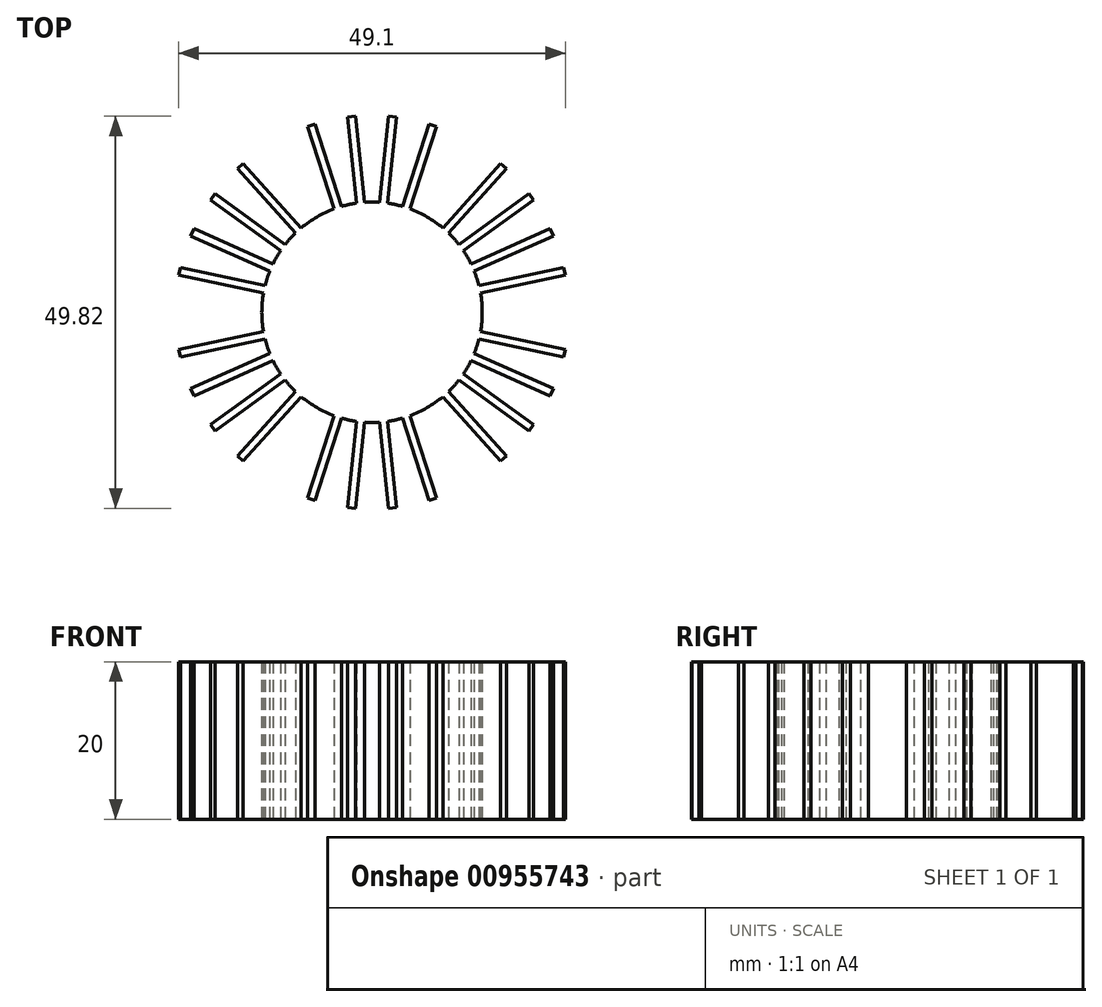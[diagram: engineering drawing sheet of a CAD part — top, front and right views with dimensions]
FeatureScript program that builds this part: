
annotation { "Feature Type Name" : "Feature", "Feature Type Description" : "" }
export const myFeature = defineFeature(function(context is Context, id is Id, definition is map)
    precondition{}
    {
        {
            var Q0;
            Q0=qCreatedBy(makeId("Top.planeOp"),FACE);
            var sketch = newSketch(context, id + "F0", { "sketchPlane" : qUnion([Q0])});
            skCircle(sketch, "E0", {"center": v(0, 0) * mm, "radius": 14 * mm});
            skLineSegment(sketch, "E1.bottom", {"start": v(0.97, 13.97) * mm, "end": v(1.96, 13.86) * mm});
            skLineSegment(sketch, "E1.top", {"start": v(2.12, 24.9) * mm, "end": v(3.1, 24.8) * mm});
            skLineSegment(sketch, "E1.left", {"start": v(0.97, 13.97) * mm, "end": v(2.12, 24.9) * mm});
            skLineSegment(sketch, "E1.right", {"start": v(1.96, 13.86) * mm, "end": v(3.1, 24.8) * mm});
            skLineSegment(sketch, "E2", {"start": v(0, 0) * mm, "end": v(0, 14) * mm});
            skLineSegment(sketch, "E3.1.0", {"start": v(-0.97, 13.97) * mm, "end": v(-2.12, 24.9) * mm});
            skLineSegment(sketch, "E3.1.1", {"start": v(-1.96, 13.86) * mm, "end": v(-3.1, 24.8) * mm});
            skLineSegment(sketch, "E3.1.2", {"start": v(-3.1, 24.8) * mm, "end": v(-2.12, 24.9) * mm});
            skLineSegment(sketch, "E3.2.0", {"start": v(-3.85, 13.46) * mm, "end": v(-7.25, 23.92) * mm});
            skLineSegment(sketch, "E3.2.1", {"start": v(-4.8, 13.15) * mm, "end": v(-8.2, 23.61) * mm});
            skLineSegment(sketch, "E3.2.2", {"start": v(-8.2, 23.61) * mm, "end": v(-7.25, 23.92) * mm});
            skLineSegment(sketch, "E3.4.0", {"start": v(-9, 10.73) * mm, "end": v(-16.35, 18.9) * mm});
            skLineSegment(sketch, "E3.4.1", {"start": v(-9.73, 10.06) * mm, "end": v(-17.1, 18.24) * mm});
            skLineSegment(sketch, "E3.4.2", {"start": v(-17.1, 18.24) * mm, "end": v(-16.35, 18.9) * mm});
            skLineSegment(sketch, "E3.5.0", {"start": v(-11.03, 8.63) * mm, "end": v(-19.92, 15.1) * mm});
            skLineSegment(sketch, "E3.5.1", {"start": v(-11.61, 7.82) * mm, "end": v(-20.51, 14.28) * mm});
            skLineSegment(sketch, "E3.5.2", {"start": v(-20.51, 14.28) * mm, "end": v(-19.92, 15.1) * mm});
            skLineSegment(sketch, "E3.6.0", {"start": v(-12.58, 6.15) * mm, "end": v(-22.63, 10.62) * mm});
            skLineSegment(sketch, "E3.6.1", {"start": v(-12.98, 5.23) * mm, "end": v(-23.03, 9.7) * mm});
            skLineSegment(sketch, "E3.6.2", {"start": v(-23.03, 9.7) * mm, "end": v(-22.63, 10.62) * mm});
            skLineSegment(sketch, "E3.7.0", {"start": v(-13.58, 3.4) * mm, "end": v(-24.34, 5.69) * mm});
            skLineSegment(sketch, "E3.7.1", {"start": v(-13.79, 2.42) * mm, "end": v(-24.55, 4.7) * mm});
            skLineSegment(sketch, "E3.7.2", {"start": v(-24.55, 4.7) * mm, "end": v(-24.34, 5.69) * mm});
            skLineSegment(sketch, "E3.9.0", {"start": v(-13.79, -2.42) * mm, "end": v(-24.55, -4.7) * mm});
            skLineSegment(sketch, "E3.9.1", {"start": v(-13.58, -3.4) * mm, "end": v(-24.34, -5.69) * mm});
            skLineSegment(sketch, "E3.9.2", {"start": v(-24.34, -5.69) * mm, "end": v(-24.55, -4.7) * mm});
            skLineSegment(sketch, "E3.10.0", {"start": v(-12.98, -5.23) * mm, "end": v(-23.03, -9.7) * mm});
            skLineSegment(sketch, "E3.10.1", {"start": v(-12.58, -6.15) * mm, "end": v(-22.63, -10.62) * mm});
            skLineSegment(sketch, "E3.10.2", {"start": v(-22.63, -10.62) * mm, "end": v(-23.03, -9.7) * mm});
            skLineSegment(sketch, "E3.11.0", {"start": v(-11.61, -7.82) * mm, "end": v(-20.51, -14.28) * mm});
            skLineSegment(sketch, "E3.11.1", {"start": v(-11.03, -8.63) * mm, "end": v(-19.92, -15.1) * mm});
            skLineSegment(sketch, "E3.11.2", {"start": v(-19.92, -15.1) * mm, "end": v(-20.51, -14.28) * mm});
            skLineSegment(sketch, "E3.12.0", {"start": v(-9.73, -10.06) * mm, "end": v(-17.1, -18.24) * mm});
            skLineSegment(sketch, "E3.12.1", {"start": v(-9, -10.73) * mm, "end": v(-16.35, -18.9) * mm});
            skLineSegment(sketch, "E3.12.2", {"start": v(-16.35, -18.9) * mm, "end": v(-17.1, -18.24) * mm});
            skLineSegment(sketch, "E3.14.0", {"start": v(-4.8, -13.15) * mm, "end": v(-8.2, -23.61) * mm});
            skLineSegment(sketch, "E3.14.1", {"start": v(-3.85, -13.46) * mm, "end": v(-7.25, -23.92) * mm});
            skLineSegment(sketch, "E3.14.2", {"start": v(-7.25, -23.92) * mm, "end": v(-8.2, -23.61) * mm});
            skLineSegment(sketch, "E3.15.0", {"start": v(-1.96, -13.86) * mm, "end": v(-3.1, -24.8) * mm});
            skLineSegment(sketch, "E3.15.1", {"start": v(-0.97, -13.97) * mm, "end": v(-2.12, -24.9) * mm});
            skLineSegment(sketch, "E3.15.2", {"start": v(-2.12, -24.9) * mm, "end": v(-3.1, -24.8) * mm});
            skLineSegment(sketch, "E3.16.0", {"start": v(0.97, -13.97) * mm, "end": v(2.12, -24.9) * mm});
            skLineSegment(sketch, "E3.16.1", {"start": v(1.96, -13.86) * mm, "end": v(3.1, -24.8) * mm});
            skLineSegment(sketch, "E3.16.2", {"start": v(3.1, -24.8) * mm, "end": v(2.12, -24.9) * mm});
            skLineSegment(sketch, "E3.17.0", {"start": v(3.85, -13.46) * mm, "end": v(7.25, -23.92) * mm});
            skLineSegment(sketch, "E3.17.1", {"start": v(4.8, -13.15) * mm, "end": v(8.2, -23.61) * mm});
            skLineSegment(sketch, "E3.17.2", {"start": v(8.2, -23.61) * mm, "end": v(7.25, -23.92) * mm});
            skLineSegment(sketch, "E3.19.0", {"start": v(9, -10.73) * mm, "end": v(16.35, -18.9) * mm});
            skLineSegment(sketch, "E3.19.1", {"start": v(9.73, -10.06) * mm, "end": v(17.1, -18.24) * mm});
            skLineSegment(sketch, "E3.19.2", {"start": v(17.1, -18.24) * mm, "end": v(16.35, -18.9) * mm});
            skLineSegment(sketch, "E3.20.0", {"start": v(11.03, -8.63) * mm, "end": v(19.92, -15.1) * mm});
            skLineSegment(sketch, "E3.20.1", {"start": v(11.61, -7.82) * mm, "end": v(20.51, -14.28) * mm});
            skLineSegment(sketch, "E3.20.2", {"start": v(20.51, -14.28) * mm, "end": v(19.92, -15.1) * mm});
            skLineSegment(sketch, "E3.21.0", {"start": v(12.58, -6.15) * mm, "end": v(22.63, -10.62) * mm});
            skLineSegment(sketch, "E3.21.1", {"start": v(12.98, -5.23) * mm, "end": v(23.03, -9.7) * mm});
            skLineSegment(sketch, "E3.21.2", {"start": v(23.03, -9.7) * mm, "end": v(22.63, -10.62) * mm});
            skLineSegment(sketch, "E3.22.0", {"start": v(13.58, -3.4) * mm, "end": v(24.34, -5.69) * mm});
            skLineSegment(sketch, "E3.22.1", {"start": v(13.79, -2.42) * mm, "end": v(24.55, -4.7) * mm});
            skLineSegment(sketch, "E3.22.2", {"start": v(24.55, -4.7) * mm, "end": v(24.34, -5.69) * mm});
            skLineSegment(sketch, "E3.24.0", {"start": v(13.79, 2.42) * mm, "end": v(24.55, 4.7) * mm});
            skLineSegment(sketch, "E3.24.1", {"start": v(13.58, 3.4) * mm, "end": v(24.34, 5.69) * mm});
            skLineSegment(sketch, "E3.24.2", {"start": v(24.34, 5.69) * mm, "end": v(24.55, 4.7) * mm});
            skLineSegment(sketch, "E3.25.0", {"start": v(12.98, 5.23) * mm, "end": v(23.03, 9.7) * mm});
            skLineSegment(sketch, "E3.25.1", {"start": v(12.58, 6.15) * mm, "end": v(22.63, 10.62) * mm});
            skLineSegment(sketch, "E3.25.2", {"start": v(22.63, 10.62) * mm, "end": v(23.03, 9.7) * mm});
            skLineSegment(sketch, "E3.26.0", {"start": v(11.61, 7.82) * mm, "end": v(20.51, 14.28) * mm});
            skLineSegment(sketch, "E3.26.1", {"start": v(11.03, 8.63) * mm, "end": v(19.92, 15.1) * mm});
            skLineSegment(sketch, "E3.26.2", {"start": v(19.92, 15.1) * mm, "end": v(20.51, 14.28) * mm});
            skLineSegment(sketch, "E3.27.0", {"start": v(9.73, 10.06) * mm, "end": v(17.1, 18.24) * mm});
            skLineSegment(sketch, "E3.27.1", {"start": v(9, 10.73) * mm, "end": v(16.35, 18.9) * mm});
            skLineSegment(sketch, "E3.27.2", {"start": v(16.35, 18.9) * mm, "end": v(17.1, 18.24) * mm});
            skLineSegment(sketch, "E3.anchor1", {"start": v(0, 0) * mm, "end": v(1.96, 13.86) * mm, "construction": true});
            skLineSegment(sketch, "E3.anchor2", {"start": v(0, 0) * mm, "end": v(4.8, 13.15) * mm, "construction": true});
            skLineSegment(sketch, "E4.1.29.0", {"start": v(4.8, 13.15) * mm, "end": v(8.2, 23.61) * mm});
            skLineSegment(sketch, "E4.3.29.0", {"start": v(3.85, 13.46) * mm, "end": v(7.25, 23.92) * mm});
            skLineSegment(sketch, "E4.6.29.0", {"start": v(7.25, 23.92) * mm, "end": v(8.2, 23.61) * mm});
            skLineSegment(sketch, "E5", {"start": v(2.61, 24.85) * mm, "end": v(1.46, 13.92) * mm});
            skSolve(sketch);
        }
        {
            var Q0;
            Q0 = qSketchRegion(id + "F0", true);
            extrude(context, id + "F1", {"entities" : qUnion([Q0]), "depth" : 20 * mm, "offsetDistance" : 25 * mm});
        }
    });
